# Revit family: Power-MouldedCaseDevices-GEWISS-97MSS-SWITCH_DISCONNECTOR_630_3P
name_source: partatom
category: Apparecchi elettrici
revit_build: Autodesk Revit 2016 (Build: 20161004_0715(x64)
units: mm (PartAtom-declared; Revit-internal decimal feet)

## family parameters
Condiviso = No
Host = Muro
Mantenere orientamento annotazione = Sì
Numero OmniClass = 23.80.50.00
Punto di calcolo locali = Sì
Quota connettore circolare = Usa diametro
Sempre verticale = Sì
Taglio con vuoti quando caricato = No
Tipo di parte = Normale
Titolo OmniClass = Terminals for Power Supply

## types (2) — shared parameters
Catalogue = POWER
Catalogue Range = 97 MSS
GW - Codice Electrocod = 150
IDF = f050b1da-643a-4487-a331-ba6306f31390
IDT = 818504ab-dddf-41f6-9b1f-b1da7f3704c5
Immagine tipo = GW97732.jpg
Label = MSS 630
No. of poles = 3P
Number of poles = 3P
Produttore = GEWISS S.p.A.
Rated voltage = 400V
SEO = Disconnector
Technical sheet = https://www.gewiss.com
URL = https://www.gewiss.com
Version file RFA = 18.0

## per-type parameters (varying)
| type | Descrizione | EAN code | Modello | Rated current (In) | Rated current: |
| GW97732 - SWITCH DISCONNECTOR MSS 630 3P 630A | SWITCH DISCONNECTOR MSS 630 3P 630A | 8011564211520 | GW97732 | 630A | 630A |
| GW97731 - SWITCH DISCONNECTOR MSS 630 3P 400A | SWITCH DISCONNECTOR MSS 630 3P 400A | 8011564211513 | GW97731 | 400A | 400A |
